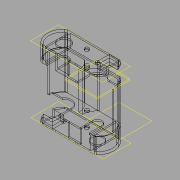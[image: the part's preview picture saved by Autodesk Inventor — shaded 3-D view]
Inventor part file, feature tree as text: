
AUTODESK INVENTOR PART (.ipt)
format: ipt  version: 2015 (Build 190159000, 159)  size: 474,624 bytes
history: native  units: mm
features: sketch x15, extrude x15, plane x8, reference x2
ambient origin geometry x8: Origin, YZ Plane, XZ Plane, XY Plane, X Axis, Y Axis, Z Axis, Center Point
bodies: Body1 (feature_tree), Body2 (feature_tree)
feature tree (40):
  sketch  "Sketch2"  dims[d13=1.0mm d14=0.0mm d15=2.0mm d16=0.0mm]
  plane  "Work Plane5"
  sketch  "Sketch5"  dims[d25=1.0mm d26=0.0mm d30=1.0mm d31=0.0mm]
  plane  "Work Plane1"
  extrude  "Extrusion3"  Depth=2.0mm TaperAngle=0.0deg
  plane  "Work Plane4"
  extrude  "Extrusion4"  Depth=1.0mm TaperAngle=0.0deg
  plane  "Work Plane6"
  sketch  "Sketch7"  dims[d47=4.0mm d48=1.0mm d49=0.0mm]
  plane  "Work Plane2"
  extrude  "Extrusion8"  Depth=8.75mm
  extrude  "Extrusion10"  Depth=1.0mm TaperAngle=0.0deg
  plane  "Work Plane12"
  plane  "Work Plane13"
  extrude  "Extrusion12"  Depth=1.0mm TaperAngle=0.0deg
  plane  "Work Plane14"
  extrude  "Extrusion13"  Depth=1.0mm TaperAngle=0.0deg
  extrude  "Extrusion14"  Depth=1.0mm TaperAngle=0.0deg
  extrude  "Extrusion15"  Depth=3.25mm TaperAngle=0.0deg
  extrude  "Extrusion16"  Depth=3.25mm TaperAngle=0.0deg
  extrude  "Extrusion17"  Depth=1.0mm
  extrude  "Extrusion18"  Depth=1.0mm
  extrude  "Extrusion19"  Depth=1.0mm TaperAngle=0.0deg
  extrude  "Extrusion20"  [1 undecoded]
  extrude  "Extrusion21"  [1 undecoded]
  extrude  "Extrusion22"  [1 undecoded]
  reference  "Reference72"
  sketch  "Sketch6"  dims[d40=8.75mm d45=8.75mm]
  sketch  "Sketch18"  dims[d50=8.75mm d52=1.0mm d53=0.0mm]
  reference  "Reference151"
  sketch  "Sketch19"  dims[d55=1.0mm d56=1.0mm d57=0.0mm]
  sketch  "Sketch21"  dims[d59=1.0mm d60=1.0mm d61=0.0mm]
  sketch  "Sketch23"  dims[d62=1.0mm d63=0.0mm d65=3.25mm d66=0.0mm]
  sketch  "Sketch24"  dims[d67=1.0mm d68=0.0mm d70=3.25mm d71=0.0mm]
  sketch  "Sketch25"  dims[d72=1.0mm d73=0.0mm d76=1.0mm]
  sketch  "Sketch26"  dims[d77=1.0mm d78=0.0mm d79=1.0mm]
  sketch  "Sketch27"  dims[d80=1.0mm d81=1.0mm d82=0.0mm]
  sketch  "Sketch28"
  sketch  "Sketch29"
  sketch  "Sketch30"
note: 3 required parameter values undecoded (feature->parameter linkage not recoverable at this tier; creation-order binding heuristic only, values carry confidence <= 0.55)
